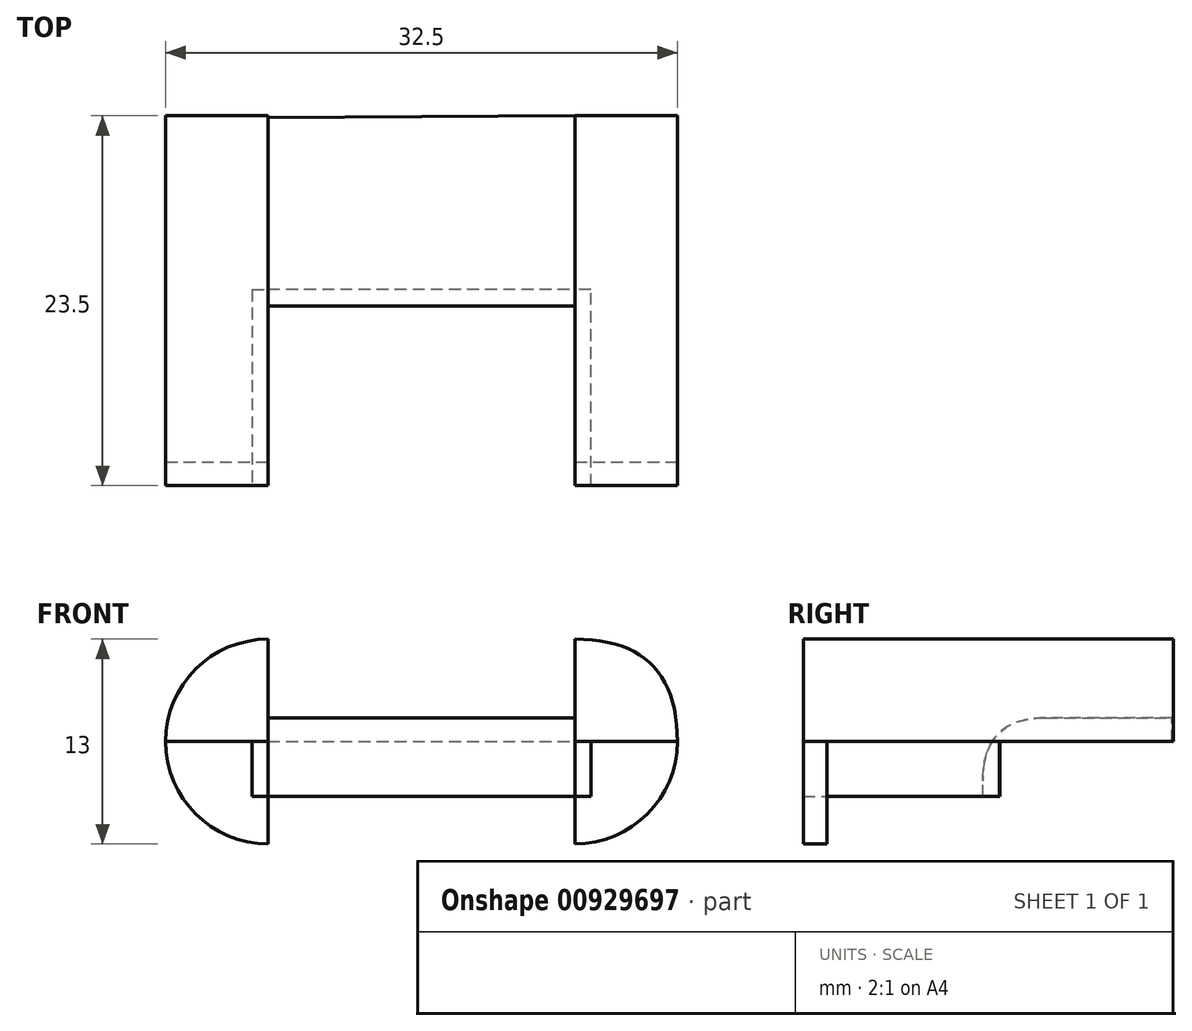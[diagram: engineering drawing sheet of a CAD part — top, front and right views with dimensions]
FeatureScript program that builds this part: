
annotation { "Feature Type Name" : "Feature", "Feature Type Description" : "" }
export const myFeature = defineFeature(function(context is Context, id is Id, definition is map)
    precondition{}
    {
        {
            var Q0;
            Q0=qCreatedBy(makeId("Top.planeOp"),FACE);
            var sketch = newSketch(context, id + "F0", { "sketchPlane" : qUnion([Q0])});
            skLineSegment(sketch, "E0.bottom", {"start": v(-16.25, 11.75) * mm, "end": v(16.25, 11.75) * mm});
            skLineSegment(sketch, "E0.top", {"start": v(-16.25, -11.75) * mm, "end": v(16.25, -11.75) * mm});
            skLineSegment(sketch, "E0.left", {"start": v(-16.25, 11.75) * mm, "end": v(-16.25, -11.75) * mm});
            skLineSegment(sketch, "E0.right", {"start": v(16.25, 11.75) * mm, "end": v(16.25, -11.75) * mm});
            skPoint(sketch, "E0.middle", {"position": v(0, 0) * mm});
            skSolve(sketch);
        }
        {
            var Q0;
            Q0 = qSketchRegion(id + "F0", true);
            extrude(context, id + "F1", {"entities" : qUnion([Q0]), "depth" : 6.5 * mm, "offsetDistance" : 25 * mm});
        }
        {
            var Q0;
            Q0=makeQuery(id+"F1.opExtrude","CAP_EDGE",EDGE,{"disambiguationData":[OSD([sQuery(id+"F0.wireOp",EDGE,"E0.right")])],"isStart":false});
            fillet(context, id + "F2", {"entities" : qUnion([Q0]), "radius" : 6.5 * mm, "tangentPropagation" : true, "rho" : 0.5, "crossSection" : FilletCrossSection.CONIC, "allowEdgeOverflow" : false});
        }
        {
            var Q0;
            Q0=makeQuery(id+"F1.opExtrude","CAP_EDGE",EDGE,{"disambiguationData":[OSD([sQuery(id+"F0.wireOp",EDGE,"E0.left")])],"isStart":false});
            fillet(context, id + "F3", {"entities" : qUnion([Q0]), "radius" : 6.5 * mm, "tangentPropagation" : true, "allowEdgeOverflow" : false});
        }
        {
            var Q0;
            Q0=makeQuery(id+"F1.opExtrude","CAP_FACE",FACE,{"disambiguationData":[OSD([sQuery(id+"F0.wireOp",EDGE,"E0.bottom"),sQuery(id+"F0.wireOp",EDGE,"E0.top"),sQuery(id+"F0.wireOp",EDGE,"E0.left"),sQuery(id+"F0.wireOp",EDGE,"E0.right")])],"isStart":false});
            extrude(context, id + "F4", {"entities" : qUnion([Q0]), "operationType" : NewBodyOperationType.REMOVE, "oppositeDirection" : true, "depth" : 6.5 * mm, "offsetDistance" : 25 * mm});
        }
        {
            var Q0;
            {var subQ0=sQuery(id+"F0.wireOp",EDGE,"E0.bottom");var subQ1=sQuery(id+"F0.wireOp",EDGE,"E0.right");var subQ2=sQuery(id+"F0.wireOp",EDGE,"E0.left");var subQ3=sQuery(id+"F0.wireOp",EDGE,"E0.top");Q0=makeQuery(id+"F4.boolean.opBoolean","SPLIT",FACE,{"disambiguationData":[TD([makeQuery(id+"F2.opFillet","BLEND_FACE",FACE,{"disambiguationData":[OSD([subQ1])]})])],"derivedFrom":makeQuery(id+"F1.opExtrude","CAP_FACE",FACE,{"disambiguationData":[OSD([subQ0,subQ3,subQ2,subQ1])],"isStart":true})});}
            var sketch = newSketch(context, id + "F5", { "sketchPlane" : qUnion([Q0])});
            skLineSegment(sketch, "E1", {"start": v(-9.75, -11.64) * mm, "end": v(9.75, -11.75) * mm});
            skLineSegment(sketch, "E2", {"start": v(-9.75, -11.64) * mm, "end": v(-9.75, 0.36) * mm});
            skLineSegment(sketch, "E3", {"start": v(-9.75, 0.36) * mm, "end": v(9.75, 0.36) * mm});
            skLineSegment(sketch, "E4", {"start": v(9.75, 0.36) * mm, "end": v(9.75, -11.75) * mm});
            skSolve(sketch);
        }
        {
            var Q0;
            Q0 = qSketchRegion(id + "F5", true);
            extrude(context, id + "F6", {"entities" : qUnion([Q0]), "operationType" : NewBodyOperationType.ADD, "depth" : 3.5 * mm, "offsetDistance" : 25 * mm});
        }
        {
            var Q0;
            {var subQ1=sQuery(id+"F0.wireOp",EDGE,"E0.left");var subQ2=sQuery(id+"F0.wireOp",EDGE,"E0.top");Q0=makeQuery(id+"F4.boolean.opBoolean","SPLIT",FACE,{"disambiguationData":[TD([makeQuery(id+"F3.opFillet","BLEND_FACE",FACE,{"disambiguationData":[OSD([subQ1])]})])],"derivedFrom":makeQuery(id+"F1.opExtrude","SWEPT_FACE",FACE,{"disambiguationData":[OSD([subQ2])]})});}
            var sketch = newSketch(context, id + "F7", { "sketchPlane" : qUnion([Q0])});
            skLineSegment(sketch, "E5", {"start": v(-16.25, 0) * mm, "end": v(-9.75, 0) * mm});
            skLineSegment(sketch, "E6", {"start": v(-9.75, 0) * mm, "end": v(-9.75, -6.5) * mm});
            skLineSegment(sketch, "E7", {"start": v(-9.75, -6.5) * mm, "end": v(-16.25, -6.5) * mm});
            skLineSegment(sketch, "E8", {"start": v(-16.25, -6.5) * mm, "end": v(-16.25, 0) * mm});
            skSolve(sketch);
        }
        {
            var Q0;
            Q0 = qSketchRegion(id + "F7", true);
            extrude(context, id + "F8", {"entities" : qUnion([Q0]), "oppositeDirection" : true, "depth" : 1.5 * mm, "offsetDistance" : 25 * mm});
        }
        {
            var Q0;
            Q0=makeQuery(id+"F8.opExtrude","SWEPT_EDGE",EDGE,{"disambiguationData":[OSD([sQuery(id+"F7.wireOp",EDGE,"E7"),sQuery(id+"F7.wireOp",EDGE,"E8")])]});
            fillet(context, id + "F9", {"entities" : qUnion([Q0]), "radius" : 6.5 * mm, "tangentPropagation" : true, "allowEdgeOverflow" : false});
        }
        {
            var Q0;
            {var subQ0=sQuery(id+"F0.wireOp",EDGE,"E0.right");var subQ2=sQuery(id+"F0.wireOp",EDGE,"E0.top");Q0=makeQuery(id+"F4.boolean.opBoolean","SPLIT",FACE,{"disambiguationData":[TD([makeQuery(id+"F2.opFillet","BLEND_FACE",FACE,{"disambiguationData":[OSD([subQ0])]})])],"derivedFrom":makeQuery(id+"F1.opExtrude","SWEPT_FACE",FACE,{"disambiguationData":[OSD([subQ2])]})});}
            var sketch = newSketch(context, id + "F10", { "sketchPlane" : qUnion([Q0])});
            skLineSegment(sketch, "E9", {"start": v(9.75, 0) * mm, "end": v(16.25, 0) * mm});
            skLineSegment(sketch, "E10", {"start": v(16.25, 0) * mm, "end": v(16.25, -6.5) * mm});
            skLineSegment(sketch, "E11", {"start": v(16.25, -6.5) * mm, "end": v(9.75, -6.5) * mm});
            skLineSegment(sketch, "E12", {"start": v(9.75, -6.5) * mm, "end": v(9.75, 0) * mm});
            skSolve(sketch);
        }
        {
            var Q0;
            Q0 = qSketchRegion(id + "F10", true);
            extrude(context, id + "F11", {"entities" : qUnion([Q0]), "oppositeDirection" : true, "depth" : 1.5 * mm, "offsetDistance" : 25 * mm});
        }
        {
            var Q0;
            Q0=makeQuery(id+"F11.opExtrude","SWEPT_EDGE",EDGE,{"disambiguationData":[OSD([sQuery(id+"F10.wireOp",EDGE,"E10"),sQuery(id+"F10.wireOp",EDGE,"E11")])]});
            fillet(context, id + "F12", {"entities" : qUnion([Q0]), "radius" : 6.5 * mm, "tangentPropagation" : true, "allowEdgeOverflow" : false});
        }
        {
            var Q0;
            Q0 = qSketchRegion(id + "F5", true);
            extrude(context, id + "F13", {"entities" : qUnion([Q0]), "operationType" : NewBodyOperationType.ADD, "oppositeDirection" : true, "depth" : 1.5 * mm, "offsetDistance" : 25 * mm});
        }
        {
            var Q0;
            Q0=makeQuery(id+"F13.opExtrude","CAP_EDGE",EDGE,{"disambiguationData":[OSD([sQuery(id+"F5.wireOp",EDGE,"E3")])],"isStart":false});
            fillet(context, id + "F14", {"entities" : qUnion([Q0]), "radius" : 4 * mm, "tangentPropagation" : true, "rho" : 0.5, "crossSection" : FilletCrossSection.CONIC, "allowEdgeOverflow" : false});
        }
        {
            var Q0;
            Q0=makeQuery(id+"F6.opExtrude","CAP_FACE",FACE,{"disambiguationData":[OSD([sQuery(id+"F5.wireOp",EDGE,"E1"),sQuery(id+"F5.wireOp",EDGE,"E2"),sQuery(id+"F5.wireOp",EDGE,"E3"),sQuery(id+"F5.wireOp",EDGE,"E4")])],"isStart":false});
            var sketch = newSketch(context, id + "F15", { "sketchPlane" : qUnion([Q0])});
            skLineSegment(sketch, "E13.bottom", {"start": v(-9.75, -0.75) * mm, "end": v(9.75, -0.75) * mm});
            skLineSegment(sketch, "E13.top", {"start": v(-9.75, -11.75) * mm, "end": v(9.75, -11.75) * mm});
            skLineSegment(sketch, "E13.left", {"start": v(-9.75, -0.75) * mm, "end": v(-9.75, -11.75) * mm});
            skLineSegment(sketch, "E13.right", {"start": v(9.75, -0.75) * mm, "end": v(9.75, -11.75) * mm});
            skSolve(sketch);
        }
        {
            var Q0;
            Q0 = qSketchRegion(id + "F15", true);
            extrude(context, id + "F16", {"entities" : qUnion([Q0]), "operationType" : NewBodyOperationType.REMOVE, "oppositeDirection" : true, "depth" : 3.5 * mm, "offsetDistance" : 25 * mm});
        }
        {
            var Q0;
            {var subQ0=sQuery(id+"F0.wireOp",EDGE,"E0.right");var subQ1=sQuery(id+"F0.wireOp",EDGE,"E0.left");var subQ2=sQuery(id+"F0.wireOp",EDGE,"E0.top");var subQ3=sQuery(id+"F0.wireOp",EDGE,"E0.bottom");Q0=makeQuery(id+"F4.boolean.opBoolean","COPY",FACE,{"derivedFrom":makeQuery(id+"F4.opExtrude","SWEPT_FACE",FACE,{"disambiguationData":[OSD([subQ3,subQ2,subQ1,subQ0]),TDD([makeQuery(id+"F3.opFillet","BLEND_EDGE",EDGE,{"blendedFrom":[makeQuery(id+"F1.opExtrude","CAP_EDGE",EDGE,{"disambiguationData":[OSD([subQ1])],"isStart":false}),makeQuery(id+"F1.opExtrude","CAP_FACE",FACE,{"disambiguationData":[OSD([subQ3,subQ2,subQ1,subQ0])],"isStart":false})],"blendedInto":[makeQuery(id+"F1.opExtrude","CAP_FACE",FACE,{"disambiguationData":[OSD([subQ3,subQ2,subQ1,subQ0])],"isStart":false})]})])]})});}
            var sketch = newSketch(context, id + "F17", { "sketchPlane" : qUnion([Q0])});
            skLineSegment(sketch, "E14.bottom", {"start": v(-11.75, 0) * mm, "end": v(0.7, 0) * mm});
            skLineSegment(sketch, "E14.top", {"start": v(-11.75, -3.5) * mm, "end": v(0.7, -3.5) * mm});
            skLineSegment(sketch, "E14.left", {"start": v(-11.75, 0) * mm, "end": v(-11.75, -3.5) * mm});
            skLineSegment(sketch, "E14.right", {"start": v(0.7, 0) * mm, "end": v(0.7, -3.5) * mm});
            skSolve(sketch);
        }
        {
            var Q0;
            Q0 = qSketchRegion(id + "F17", true);
            extrude(context, id + "F18", {"entities" : qUnion([Q0]), "oppositeDirection" : true, "depth" : 1 * mm, "offsetDistance" : 25 * mm});
        }
        {
            var Q0;
            {var subQ0=sQuery(id+"F0.wireOp",EDGE,"E0.right");var subQ1=sQuery(id+"F0.wireOp",EDGE,"E0.left");var subQ2=sQuery(id+"F0.wireOp",EDGE,"E0.top");var subQ3=sQuery(id+"F0.wireOp",EDGE,"E0.bottom");Q0=makeQuery(id+"F4.boolean.opBoolean","COPY",FACE,{"derivedFrom":makeQuery(id+"F4.opExtrude","SWEPT_FACE",FACE,{"disambiguationData":[OSD([subQ3,subQ2,subQ1,subQ0]),TDD([makeQuery(id+"F2.opFillet","BLEND_EDGE",EDGE,{"blendedFrom":[makeQuery(id+"F1.opExtrude","CAP_EDGE",EDGE,{"disambiguationData":[OSD([subQ0])],"isStart":false}),makeQuery(id+"F1.opExtrude","CAP_FACE",FACE,{"disambiguationData":[OSD([subQ3,subQ2,subQ1,subQ0])],"isStart":false})],"blendedInto":[makeQuery(id+"F1.opExtrude","CAP_FACE",FACE,{"disambiguationData":[OSD([subQ3,subQ2,subQ1,subQ0])],"isStart":false})]})])]})});}
            var sketch = newSketch(context, id + "F19", { "sketchPlane" : qUnion([Q0])});
            skLineSegment(sketch, "E15.bottom", {"start": v(11.75, 0) * mm, "end": v(-0.7, 0) * mm});
            skLineSegment(sketch, "E15.top", {"start": v(11.75, -3.5) * mm, "end": v(-0.7, -3.5) * mm});
            skLineSegment(sketch, "E15.left", {"start": v(11.75, 0) * mm, "end": v(11.75, -3.5) * mm});
            skLineSegment(sketch, "E15.right", {"start": v(-0.7, 0) * mm, "end": v(-0.7, -3.5) * mm});
            skSolve(sketch);
        }
        {
            var Q0;
            Q0 = qSketchRegion(id + "F19", true);
            extrude(context, id + "F20", {"entities" : qUnion([Q0]), "oppositeDirection" : true, "depth" : 1 * mm, "offsetDistance" : 25 * mm});
        }
    });
